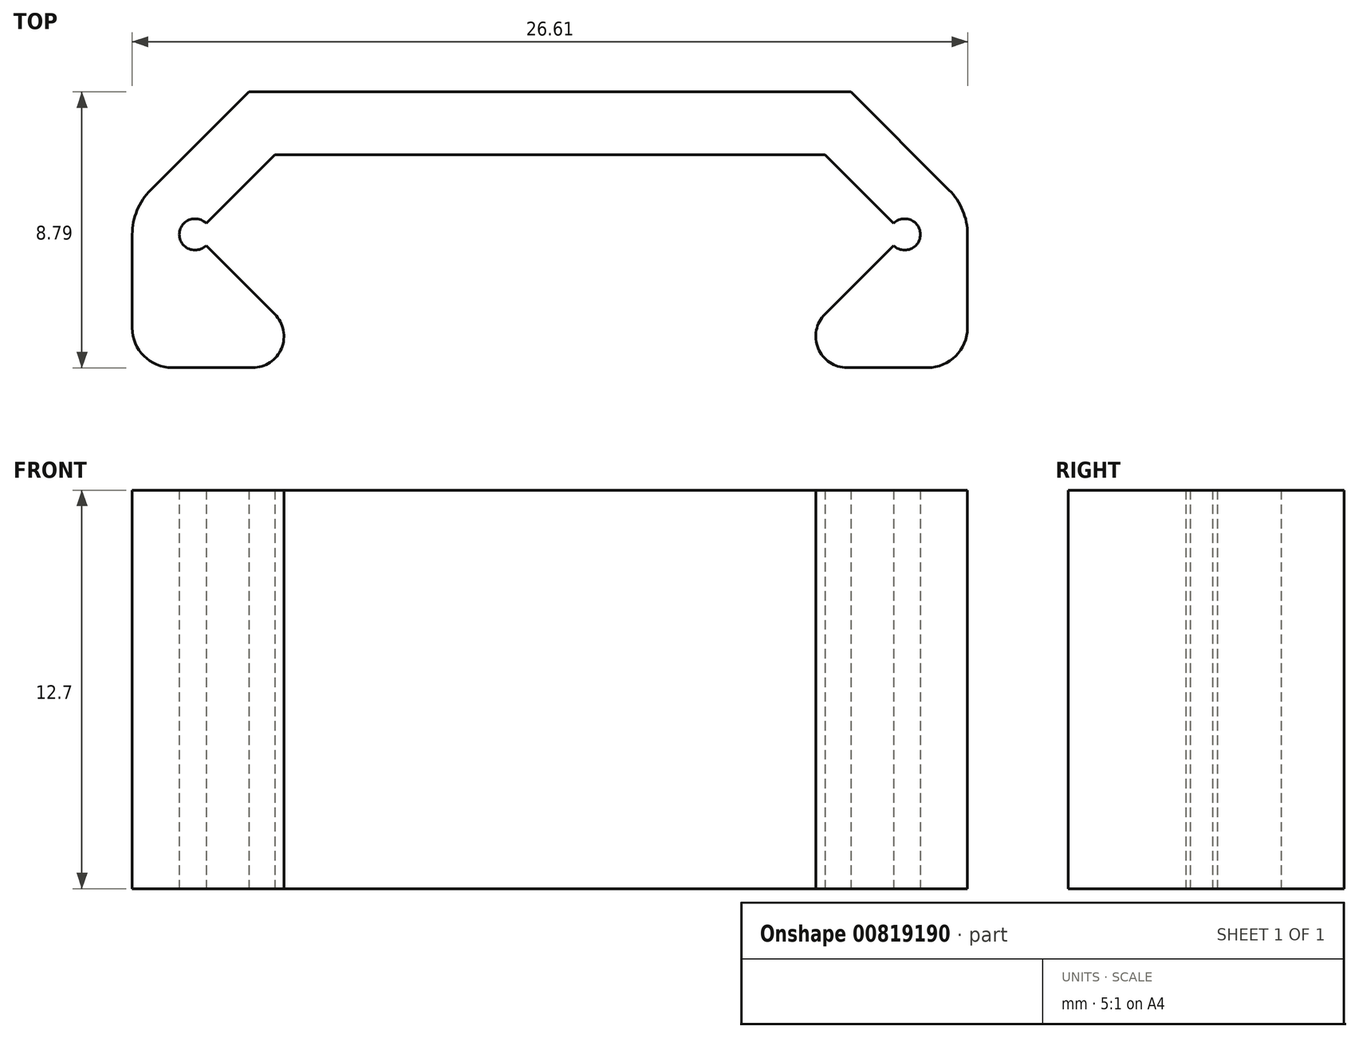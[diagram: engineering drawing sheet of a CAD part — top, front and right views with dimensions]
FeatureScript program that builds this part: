
annotation { "Feature Type Name" : "Feature", "Feature Type Description" : "" }
export const myFeature = defineFeature(function(context is Context, id is Id, definition is map)
    precondition{}
    {
        {
            var Q0;
            Q0=qCreatedBy(makeId("Top.planeOp"),FACE);
            var sketch = newSketch(context, id + "F0", { "sketchPlane" : qUnion([Q0])});
            skLineSegment(sketch, "E0.top", {"start": v(0.35, 0.35) * mm, "end": v(2.54, 2.54) * mm});
            skLineSegment(sketch, "E0.left", {"start": v(2.54, -2.54) * mm, "end": v(0.35, -0.35) * mm});
            skLineSegment(sketch, "E1.top", {"start": v(20.07, 2.54) * mm, "end": v(22.25, 0.35) * mm});
            skLineSegment(sketch, "E1.right", {"start": v(20.07, -2.54) * mm, "end": v(22.25, -0.35) * mm});
            skLineSegment(sketch, "E2.2", {"start": v(-1.41, 1.41) * mm, "end": v(1.71, 4.54) * mm});
            skLineSegment(sketch, "E2.4", {"start": v(20.9, 4.54) * mm, "end": v(24.02, 1.41) * mm});
            skArc(sketch, "E3", {"start": v(0.35, 0.35) * mm, "mid": v(-0.5, 0) * mm, "end": v(0.35, -0.35) * mm});
            skArc(sketch, "E4", {"start": v(22.25, -0.35) * mm, "mid": v(23.1, 0) * mm, "end": v(22.25, 0.35) * mm});
            skArc(sketch, "E5", {"start": v(24.6, 0) * mm, "mid": v(24.45, 0.77) * mm, "end": v(24.02, 1.41) * mm});
            skArc(sketch, "E6", {"start": v(-1.41, 1.41) * mm, "mid": v(-1.85, 0.77) * mm, "end": v(-2, 0) * mm});
            skArc(sketch, "E7", {"start": v(1.83, -4.25) * mm, "mid": v(2.76, -3.63) * mm, "end": v(2.54, -2.54) * mm});
            skArc(sketch, "E8", {"start": v(20.07, -2.54) * mm, "mid": v(19.85, -3.63) * mm, "end": v(20.77, -4.25) * mm});
            skLineSegment(sketch, "E9", {"start": v(1.83, -4.25) * mm, "end": v(-0.73, -4.25) * mm});
            skLineSegment(sketch, "E10", {"start": v(20.77, -4.25) * mm, "end": v(23.34, -4.25) * mm});
            skLineSegment(sketch, "E11", {"start": v(-2, 0) * mm, "end": v(-2, -2.98) * mm});
            skLineSegment(sketch, "E12", {"start": v(24.6, 0) * mm, "end": v(24.6, -2.98) * mm});
            skPoint(sketch, "E2.1.start.orphan", {"position": v(1.13, -3.95) * mm});
            skPoint(sketch, "E13.orphan", {"position": v(21.48, -3.95) * mm});
            skPoint(sketch, "E14.visualSharp", {"position": v(-2, -4.25) * mm});
            skArc(sketch, "E14.filletArc", {"start": v(-2, -2.98) * mm, "mid": v(-1.63, -3.88) * mm, "end": v(-0.73, -4.25) * mm});
            skPoint(sketch, "E15.visualSharp", {"position": v(24.6, -4.25) * mm});
            skArc(sketch, "E15.filletArc", {"start": v(23.34, -4.25) * mm, "mid": v(24.23, -3.88) * mm, "end": v(24.6, -2.98) * mm});
            skLineSegment(sketch, "E16", {"start": v(11.7, 2.54) * mm, "end": v(20.07, 2.54) * mm});
            skLineSegment(sketch, "E17", {"start": v(11.7, 2.54) * mm, "end": v(2.54, 2.54) * mm});
            skLineSegment(sketch, "E18.0", {"start": v(11.7, 4.54) * mm, "end": v(1.71, 4.54) * mm});
            skLineSegment(sketch, "E18.1", {"start": v(11.7, 4.54) * mm, "end": v(20.9, 4.54) * mm});
            skSolve(sketch);
        }
        {
            var Q0;
            Q0=qSketchRegion(id+"F0",true);
            extrude(context, id + "F1", {"entities" : qUnion([Q0]), "depth" : 12.7 * mm, "offsetDistance" : 25.4 * mm});
        }
    });
